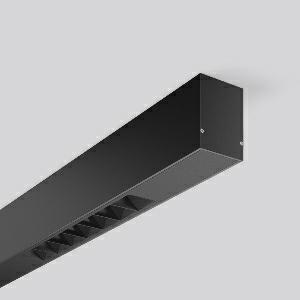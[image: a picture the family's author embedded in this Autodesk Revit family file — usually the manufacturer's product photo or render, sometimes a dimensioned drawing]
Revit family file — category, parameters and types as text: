
# Revit family: less_is_more_beamline_312486_003_5b91
name_source: partatom
category: Lighting Fixtures
units: mm (PartAtom-declared; Revit-internal decimal feet)

## family parameters
Cut with Voids When Loaded = No
Host = Face
Light Source = No
Part Type = Normal
Room Calculation Point = No
Round Connector Dimension = Use Diameter
Shared = No

## types (1)
- LESS IS MORE BEAMLINE (1 x LED Modul 930, 1800 lm, 3000)
    Apparent Load = 48 VA
    CIE Flux Codes = 100 100 100 100 100
    Color Rendering = 90
    Color Temperature = 3000
    Default Elevation = 1800 mm  [stored 5.90551 ft]
    Description = Series: LESS IS MORE BEAMLINE
Linear ceiling and wall luminaire for aesthetically sophisticated lighting. Luminaire with two LED light units. Housing: extruded aluminium profile, powder-coated. End cap aluminium powder-coated. LED light unit with MRS technology: Mini-Reflector-System made of metallised thermoplastic with prismatic black glare-suppressing frame for pleasant glare-free light (RUG < 10). Each LED light unit has 7 reflector elements. Narrow beam light distribution. LED unit with integrated converter interchangeable and removable. Suitable for through-wiring. 
Colour: deep black, matt (RAL 9005)
Length: 1127 mm
Width: 57 mm
Height: 75 mm
Lamp: LED
Socket: without socket
Colour temperature: 3000K
Colour rendering index (CRI): 90
System power: 48 W
Rated luminous flux: 3600 lm
Luminous efficiency: 75 lm/W
Control gear: Regulated power supply
Protection class: I
Type of protection: IP 20
    Height = 75 mm
    Lamp = 1 x LED Modul 930
    Lamp Light Flux = 1800 lm
    Lamp count = 1
    Length = 1127 mm
    Lifetime = 50000 h
    Luminous efficacy = 75 lm/W
    Manufacturer = RZB
    ModVariant = No
    Model = 312486.003
    Mounting Place = Ceiling, Wall
    Mounting Type = Surface mounted
    Number of Poles = 1
    OnlyDefault = Yes
    Power Factor = 1
    Product Name = LESS IS MORE BEAMLINE
    Product group = Surface mounted LED linear luminaires
    ProductGroupID = 307
    Protection Class = Protection class I
    Protection Degree = IP 20
    RLX_Detail_Level = 1
    RLX_Emergency_Light_Flux = 0 lm
    RLX_Emergency_Type = 0
    RLX_Emergency_Type_DB = No
    RlxData = <blob elided: 29849 chars, md5=1a3cc543>
    Socket = socket
    Standby Power = 0 W
    System Light Flux = 3600 lm
    System Power = 48 W
    Type Comments = Product without accessories
    Type Image = 312483.003.jpg
    URL = http://relux.com
    VarID = ---
    Voltage = 230 V
    Voltage Range = 220-240 V
    Weight = 0.00 kg
    Width = 57 mm

note: [stored X ft] marks values corroborated as IEEE doubles in the binary element streams (Revit-internal decimal feet)

## geometry (parser evidence)
native form markers: Blend x4, Sweep x16
no freeform markers — native parametric forms only
